# Revit family: plumbing-fixture-grohe-Eurosmart-Cosmopolitan-basin-mixer-328240001
name_source: partatom
category: Plumbing Fixtures
revit_build: Autodesk Revit 2013 (Build: 20130531_2115(x64)
units: mm (PartAtom-declared; Revit-internal decimal feet)

## types (1)
- Eurosmart 328 240 00
    ADA Compliant = Yes
    Assembly Code = C1030220
    AssetType = Fixed
    Barcode = 0
    CW Connection = Yes
    CWFU = 4.5
    Cold Water Connection Diameter = 10 mm  [stored 0.0328084 ft]
    Cold Water Radius = 5 mm  [stored 0.0164042 ft]
    Cost = 0 $
    Default Elevation = 600 mm
    Ecojoy = Yes
    ExpectedLife = 0
    Faucet Material = Grohe-Chrome
    Flow Pressure = min 0.05MPa/recommended 0.1 - 0.6MPa
    Flow Rate = approx 6 L/min
    HW Connection = Yes
    HWFU = 4.5
    Height = 148 mm  [stored 0.485564 ft]
    Hot Water Connection Diameter = 10 mm  [stored 0.0328084 ft]
    Hot Water Radius = 5 mm  [stored 0.0164042 ft]
    Keynote = N13
    Length = 92 mm  [stored 0.301837 ft]
    Low Emitting Material = Yes
    Manufacturer = Grohe AG
    Manufacturers Telephone Number = 08712003414
    Mixing Leaver = Yes
    Model = Eurosmart 32824000
    ModelNumber = Eurosmart 32824000
    Name = Eurosmart 32824000
    Operating Pressure = max 1MPa
    Percentage of Recycled Content = 0
    Product Documentation Link = http://cdn08.grohe.com
    TagNumber = 0
    Temp - Hot Water Supply = max 70 deg C
    Temp - Hot Water Supply (Recommended) = 60 deg C
    URL = www.grohe.com
    Vent Connection = No
    Version = 0
    WFU = 0
    Waste Connection = No
    Width = 34 mm
    _BIMspec_GUID = 0
    _current revision = 1
    _distributed by = www.bimstore.co.uk

note: [stored X ft] marks values corroborated as IEEE doubles in the binary element streams (Revit-internal decimal feet)

## geometry (parser evidence)
native form markers: Blend x4, Sweep x1
no freeform markers — native parametric forms only
